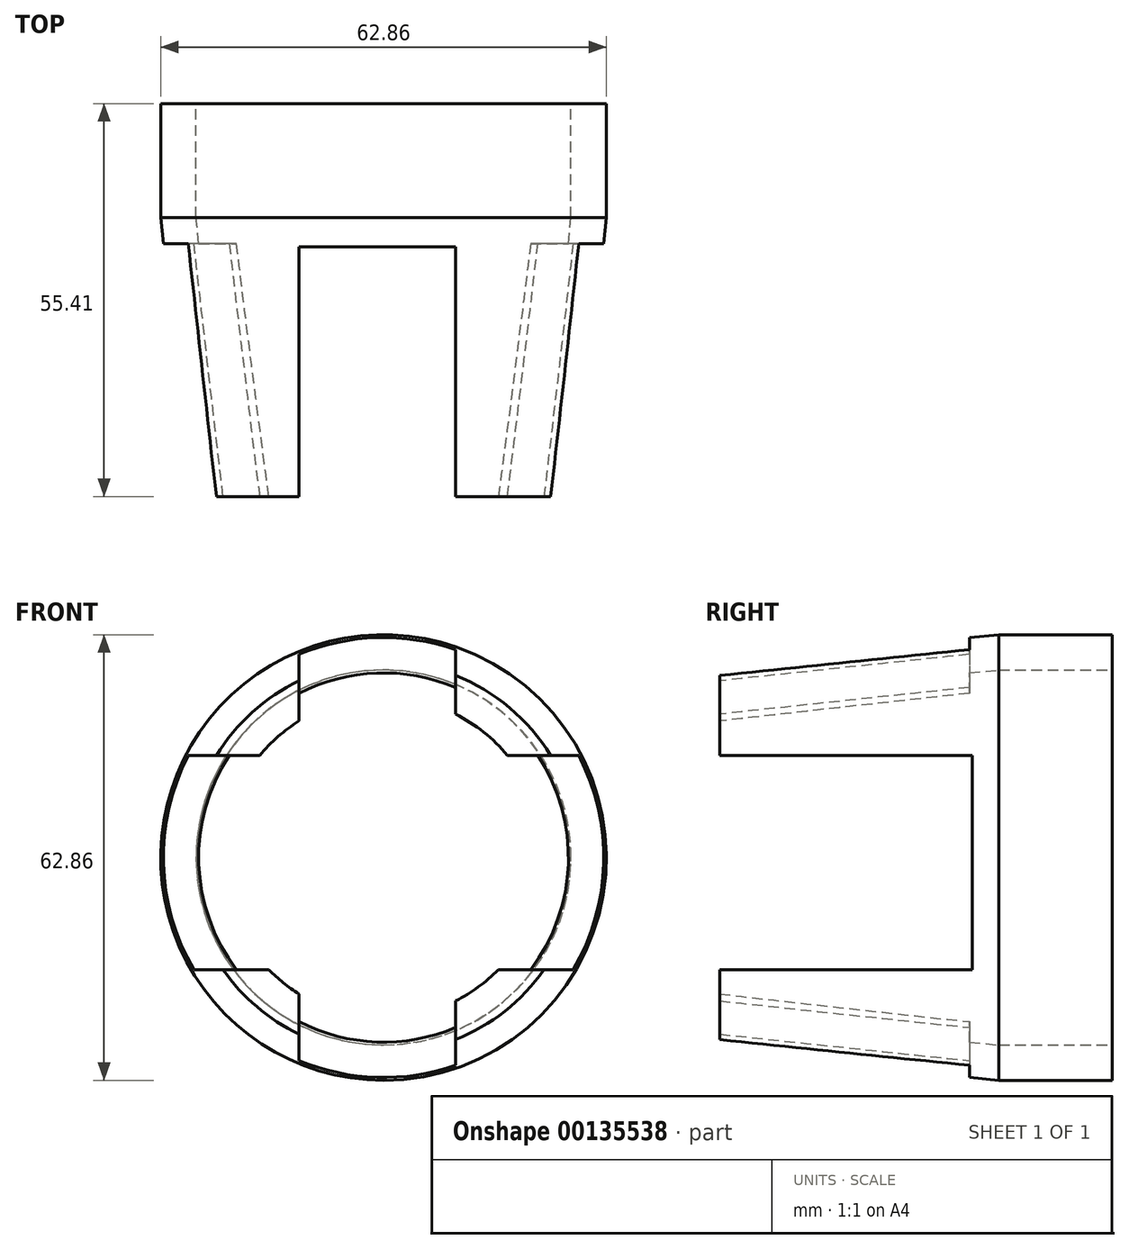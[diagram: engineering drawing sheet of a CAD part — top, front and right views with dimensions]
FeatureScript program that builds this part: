
annotation { "Feature Type Name" : "Feature", "Feature Type Description" : "" }
export const myFeature = defineFeature(function(context is Context, id is Id, definition is map)
    precondition{}
    {
        {
            var Q0;
            Q0=qCreatedBy(makeId("Front.planeOp"),FACE);
            var sketch = newSketch(context, id + "F0", { "sketchPlane" : qUnion([Q0])});
            skCircle(sketch, "E0", {"center": v(0, 0) * mm, "radius": 26.45 * mm});
            skSolve(sketch);
        }
        {
            var Q0;
            Q0 = qSketchRegion(id + "F0", true);
            extrude(context, id + "F1", {"entities" : qUnion([Q0]), "depth" : 55.4 * mm});
        }
        {
            var Q0;
            Q0=makeQuery(id+"F1.opExtrude","CAP_EDGE",EDGE,{"disambiguationData":[OSD([sQuery(id+"F0.wireOp",EDGE,"E0")])],"isStart":false});
            chamfer(context, id + "F2", {"entities" : qUnion([Q0]), "chamferType" : ChamferType.TWO_OFFSETS, "width1" : 3.8 * mm, "oppositeDirection" : false, "width2" : 39.37 * mm, "tangentPropagation" : true});
        }
        {
            var Q0;
            Q0=qCreatedBy(makeId("Front.planeOp"),FACE);
            var sketch = newSketch(context, id + "F3", { "sketchPlane" : qUnion([Q0])});
            skCircle(sketch, "E1", {"center": v(0, 0) * mm, "radius": 31.43 * mm});
            skSolve(sketch);
        }
        {
            var Q0;
            Q0 = qSketchRegion(id + "F3", true);
            extrude(context, id + "F4", {"entities" : qUnion([Q0]), "depth" : 55.4 * mm});
        }
        {
            var Q0;
            Q0=makeQuery(id+"F4.opExtrude","CAP_EDGE",EDGE,{"disambiguationData":[OSD([sQuery(id+"F3.wireOp",EDGE,"E1")])],"isStart":false});
            chamfer(context, id + "F5", {"entities" : qUnion([Q0]), "chamferType" : ChamferType.TWO_OFFSETS, "width1" : 3.8 * mm, "oppositeDirection" : false, "width2" : 39.37 * mm, "tangentPropagation" : true});
        }
        {
            var Q0;
            Q0=makeQuery(id+"F1.opExtrude","SWEPT_BODY",BODY,{"disambiguationData":[OSD([sQuery(id+"F0.wireOp",EDGE,"E0")])]});
            var Q1;
            Q1=makeQuery(id+"F4.opExtrude","SWEPT_BODY",BODY,{"disambiguationData":[OSD([sQuery(id+"F3.wireOp",EDGE,"E1")])]});
            booleanBodies(context, id + "F6", {"operationType" : BooleanOperationType.SUBTRACTION, "tools" : qUnion([Q0]), "targets" : qUnion([Q1])});
        }
        {
            var Q0;
            Q0=qCreatedBy(makeId("Right.planeOp"),FACE);
            var sketch = newSketch(context, id + "F7", { "sketchPlane" : qUnion([Q0])});
            skLineSegment(sketch, "E2.bottom", {"start": v(-19.75, 0) * mm, "end": v(-30.2, 0) * mm});
            skLineSegment(sketch, "E2.top", {"start": v(-19.75, 14.38) * mm, "end": v(-30.2, 14.38) * mm});
            skLineSegment(sketch, "E2.left", {"start": v(-19.75, 0) * mm, "end": v(-19.75, 14.38) * mm});
            skLineSegment(sketch, "E2.right", {"start": v(-30.2, 0) * mm, "end": v(-30.2, 14.38) * mm});
            skLineSegment(sketch, "E3.bottom", {"start": v(-30.2, 0) * mm, "end": v(-19.75, 0) * mm});
            skLineSegment(sketch, "E3.top", {"start": v(-30.2, -15.83) * mm, "end": v(-19.75, -15.83) * mm});
            skLineSegment(sketch, "E3.left", {"start": v(-30.2, 0) * mm, "end": v(-30.2, -15.83) * mm});
            skLineSegment(sketch, "E3.right", {"start": v(-19.75, 0) * mm, "end": v(-19.75, -15.83) * mm});
            skLineSegment(sketch, "E4.bottom", {"start": v(-30.2, 14.38) * mm, "end": v(-65, 14.38) * mm});
            skLineSegment(sketch, "E4.top", {"start": v(-30.2, -15.83) * mm, "end": v(-65, -15.83) * mm});
            skLineSegment(sketch, "E4.left", {"start": v(-30.2, 14.38) * mm, "end": v(-30.2, -15.83) * mm});
            skLineSegment(sketch, "E4.right", {"start": v(-65, 14.38) * mm, "end": v(-65, -15.83) * mm});
            skSolve(sketch);
        }
        {
            var Q0;
            Q0 = qSketchRegion(id + "F7", true);
            extrude(context, id + "F8", {"entities" : qUnion([Q0]), "operationType" : NewBodyOperationType.REMOVE, "depth" : 43.92 * mm, "hasSecondDirection" : true, "secondDirectionOppositeDirection" : true, "secondDirectionDepth" : 42.43 * mm});
        }
        {
            var Q0;
            Q0=qCreatedBy(makeId("Top.planeOp"),FACE);
            var sketch = newSketch(context, id + "F9", { "sketchPlane" : qUnion([Q0])});
            skLineSegment(sketch, "E5.bottom", {"start": v(-11.9, -30.06) * mm, "end": v(10.16, -30.06) * mm});
            skLineSegment(sketch, "E5.top", {"start": v(-11.9, -20.18) * mm, "end": v(10.16, -20.18) * mm});
            skLineSegment(sketch, "E5.left", {"start": v(-11.9, -30.06) * mm, "end": v(-11.9, -20.18) * mm});
            skLineSegment(sketch, "E5.right", {"start": v(10.16, -30.06) * mm, "end": v(10.16, -20.18) * mm});
            skLineSegment(sketch, "E6.top", {"start": v(-11.9, -61.61) * mm, "end": v(10.16, -61.61) * mm});
            skLineSegment(sketch, "E6.left", {"start": v(-11.9, -30.06) * mm, "end": v(-11.9, -61.61) * mm});
            skLineSegment(sketch, "E6.right", {"start": v(10.16, -30.06) * mm, "end": v(10.16, -61.61) * mm});
            skSolve(sketch);
        }
        {
            var Q0;
            Q0 = qSketchRegion(id + "F9", true);
            extrude(context, id + "F10", {"entities" : qUnion([Q0]), "operationType" : NewBodyOperationType.REMOVE, "depth" : 52.7 * mm, "hasSecondDirection" : true, "secondDirectionOppositeDirection" : true, "secondDirectionDepth" : 50.38 * mm});
        }
    });
